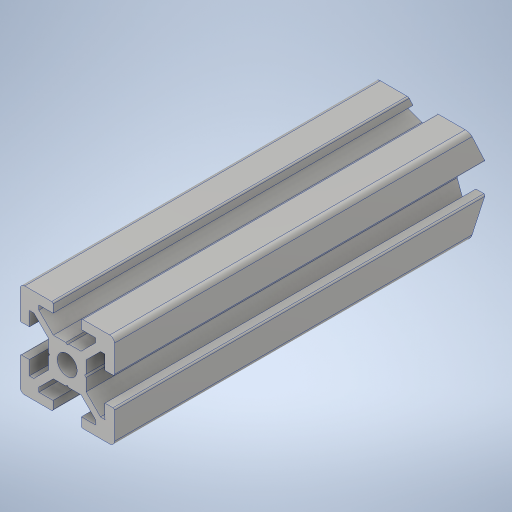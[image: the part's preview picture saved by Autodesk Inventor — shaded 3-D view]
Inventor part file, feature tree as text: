
AUTODESK INVENTOR PART (.ipt)
format: ipt  version: 2024 (Build 280153000, 153)  size: 398,848 bytes
history: native  units: mm
features: other x7, sketch x3, extrude x2, hole x1
ambient origin geometry x8: Origin, YZ Plane, XZ Plane, XY Plane, X Axis, Y Axis, Z Axis, Center Point
bodies: Solid1 (feature_tree)
feature tree (13):
  extrude  "Extrusion1"  TaperAngle=0.0deg  [1 undecoded]
  other  "to_frame_XY"
  other  "to_frame_YZ"
  other  "to_frame_ZX"
  other  "to_frame_X"
  other  "to_frame_Y"
  other  "to_frame_Z"
  other  "to_frame_Center"
  hole  "구멍1"  [1 undecoded]
  extrude  "돌출2"  Depth=8.0mm
  sketch  "Sketch_5"  dims[d0=80.0mm d1=0.0mm d2=0.0mm d3=5.0mm d4=4.0mm d5=6.0mm d6=4.0mm d7=2.0mm d8=90.0deg d9=8.0mm d10=20.594885mm d11=4.363323mm d12=11.34464mm d13=0.0mm d14=0.0mm d15=0.5mm d16=0.872665mm]
  sketch  "스케치2"
  sketch  "스케치3"
note: 2 required parameter values undecoded (feature->parameter linkage not recoverable at this tier; creation-order binding heuristic only, values carry confidence <= 0.55)
